# Revit family: Plumbing_Drainage-Zurn-Z1761_Kettle-Drain
name_source: partatom
category: Plumbing Fixtures
units: mm (PartAtom-declared; Revit-internal decimal feet)

## family parameters
Always vertical = Yes
Cut with Voids When Loaded = No
Maintain Annotation Orientation = No
OmniClass Number = 23.45.55.21
OmniClass Title = Drains (Wastes)
Part Type = Normal
Room Calculation Point = No
Round Connector Dimension = Use Radius
Shared = No
Work Plane-Based = No

## types (9) — shared parameters
Approx. Wt. Lbs = 72 "
Assembly Code = D2030300
CW Connection = No
Description = 24 5/16  [618] SQUARE KETTLE DRAIN W/ 8 [203] SUMP DEPTH
HW Connection = No
Main Material = Steel - Zurn - Stainless - A.R.E Coated - Type - 304
Manufacturer = Zurn Water, LLC
Manufacturer Brand = Zurn
Model = Z1761
Modified Date = 09/02/2025
Product Documentation Link = https://files.zurn.com
Product Page URL = https://www.zurn.com
Product data URL = https://www.bimobject.com
URL = www.zurn.com
Vent Connection = No
WFU = 1
Waste Connection = Yes
zero-valued in all types: CWFU, Default Elevation, Grate Open Area, HWFU

## per-type parameters (varying)
| type | C | Grate Material | Pipe Size A (Actual Radius) | Pipe Size A (Diameter) | Pipe Size A (Nominal Radius) | Type Comments | x |
| Z1761-4NH Outlet | 24.016 " | Steel - Zurn - Stainless - Type - 304 | 2.25 " | 4 " | 2 " | Z1761 4 Inch No-Hub Outlet | 24.331 " |
| Z1761-6NH Outlet | 24.016 " | Steel - Zurn - Stainless - Type - 304 | 3.313 " | 6 " | 3 " | Z1761 6 Inch No-Hub Outlet | 24.331 " |
| Z1761-8NH Outlet | 24 " | Steel - Zurn - Stainless - Type - 304 | 4.313 " | 8 " | 4 " | Z1761 8 Inch No-Hub Outlet | 24.313 " |
| ZM1761-4NH Outlet | 24.016 " | Steel - Zurn - Stainless - Type - 316 | 2.25 " | 4 " | 2 " | ZM1761 4 Inch No-Hub Outlet | 24.331 " |
| ZM1761-6NH Outlet | 24.016 " | Steel - Zurn - Stainless - Type - 316 | 3.313 " | 6 " | 3 " | ZM1761 6 Inch No-Hub Outlet | 24.331 " |
| ZM1761-8NH Outlet | 24.016 " | Steel - Zurn - Stainless - Type - 316 | 4.313 " | 8 " | 4 " | ZM1761 8 Inch No-Hub Outlet | 24.331 " |
| ZS1761-4NH Outlet | 24.016 " | Steel - Zurn - Stainless - Type - 304 | 2.25 " | 4 " | 2 " | ZS1761 4 Inch No-Hub Outlet | 24.331 " |
| ZS1761-6NH Outlet | 24.016 " | Steel - Zurn - Stainless - Type - 304 | 3.313 " | 6 " | 3 " | ZS1761 6 Inch No-Hub Outlet | 24.331 " |
| ZS1761-8NH Outlet | 24.016 " | Steel - Zurn - Stainless - Type - 304 | 4.313 " | 8 " | 4 " | ZS1761 8 Inch No-Hub Outlet | 24.331 " |

## geometry (parser evidence)
native form markers: Sweep x2
no freeform markers — native parametric forms only
